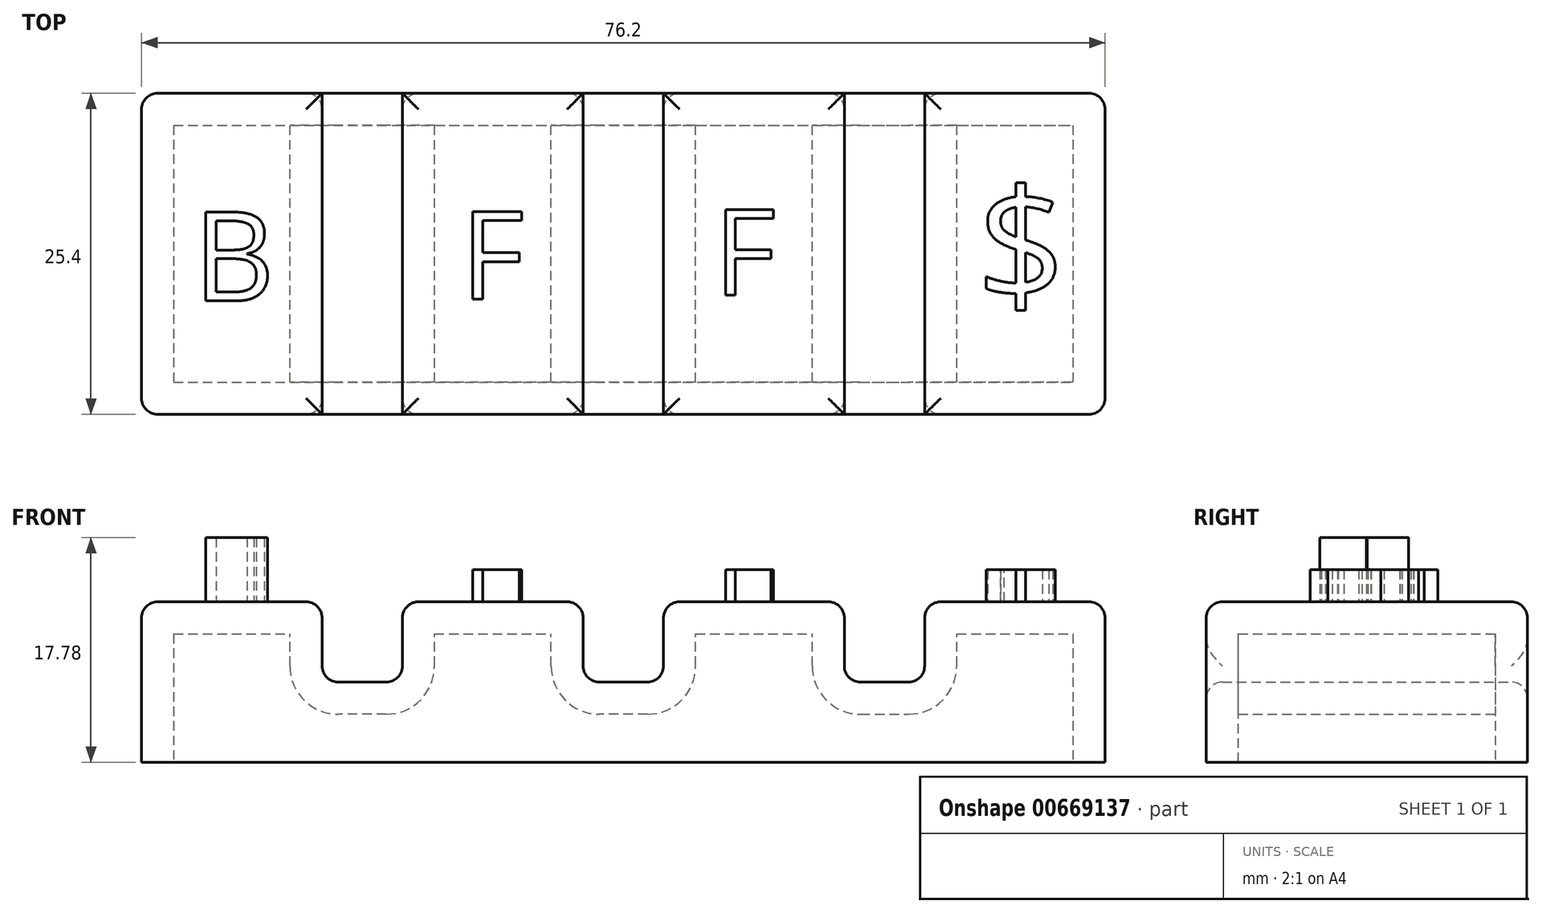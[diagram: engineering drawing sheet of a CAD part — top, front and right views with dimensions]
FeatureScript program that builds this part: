
annotation { "Feature Type Name" : "Feature", "Feature Type Description" : "" }
export const myFeature = defineFeature(function(context is Context, id is Id, definition is map)
    precondition{}
    {
        {
            var Q0;
            Q0=qCreatedBy(makeId("Top.planeOp"),FACE);
            var sketch = newSketch(context, id + "F0", { "sketchPlane" : qUnion([Q0])});
            skLineSegment(sketch, "E0.bottom", {"start": v(-38.1, 12.7) * mm, "end": v(38.1, 12.7) * mm});
            skLineSegment(sketch, "E0.top", {"start": v(-38.1, -12.7) * mm, "end": v(38.1, -12.7) * mm});
            skLineSegment(sketch, "E0.left", {"start": v(-38.1, 12.7) * mm, "end": v(-38.1, -12.7) * mm});
            skLineSegment(sketch, "E0.right", {"start": v(38.1, 12.7) * mm, "end": v(38.1, -12.7) * mm});
            skPoint(sketch, "E0.middle", {"position": v(0, 0) * mm});
            skSolve(sketch);
        }
        {
            var Q0;
            Q0 = qSketchRegion(id + "F0", true);
            extrude(context, id + "F1", {"entities" : qUnion([Q0]), "depth" : 12.7 * mm, "offsetDistance" : 25.4 * mm});
        }
        {
            var Q0;
            Q0=makeQuery(id+"F1.opExtrude","SWEPT_FACE",FACE,{"disambiguationData":[OSD([sQuery(id+"F0.wireOp",EDGE,"E0.bottom")])]});
            var sketch = newSketch(context, id + "F2", { "sketchPlane" : qUnion([Q0])});
            skLineSegment(sketch, "E1", {"start": v(-38.1, 6.35) * mm, "end": v(38.1, 6.35) * mm, "construction": true});
            skLineSegment(sketch, "E2.bottom", {"start": v(3.17, 6.35) * mm, "end": v(-3.18, 6.35) * mm});
            skLineSegment(sketch, "E2.top", {"start": v(3.17, 19.05) * mm, "end": v(-3.18, 19.05) * mm});
            skLineSegment(sketch, "E2.left", {"start": v(3.17, 6.35) * mm, "end": v(3.17, 19.05) * mm});
            skLineSegment(sketch, "E2.right", {"start": v(-3.18, 6.35) * mm, "end": v(-3.18, 19.05) * mm});
            skPoint(sketch, "E2.middle", {"position": v(0, 12.7) * mm});
            skLineSegment(sketch, "E3.bottom", {"start": v(23.83, 6.35) * mm, "end": v(17.48, 6.35) * mm});
            skLineSegment(sketch, "E3.top", {"start": v(23.83, 19.05) * mm, "end": v(17.48, 19.05) * mm});
            skLineSegment(sketch, "E3.left", {"start": v(23.83, 6.35) * mm, "end": v(23.83, 19.05) * mm});
            skLineSegment(sketch, "E3.right", {"start": v(17.48, 6.35) * mm, "end": v(17.48, 19.05) * mm});
            skPoint(sketch, "E3.middle", {"position": v(20.65, 12.7) * mm});
            skLineSegment(sketch, "E4.bottom", {"start": v(-23.83, 6.35) * mm, "end": v(-17.48, 6.35) * mm});
            skLineSegment(sketch, "E4.top", {"start": v(-23.83, 19.05) * mm, "end": v(-17.48, 19.05) * mm});
            skLineSegment(sketch, "E4.left", {"start": v(-23.83, 6.35) * mm, "end": v(-23.83, 19.05) * mm});
            skLineSegment(sketch, "E4.right", {"start": v(-17.48, 6.35) * mm, "end": v(-17.48, 19.05) * mm});
            skPoint(sketch, "E4.middle", {"position": v(-20.65, 12.7) * mm});
            skSolve(sketch);
        }
        {
            var Q0;
            Q0 = qSketchRegion(id + "F2", true);
            extrude(context, id + "F3", {"entities" : qUnion([Q0]), "operationType" : NewBodyOperationType.REMOVE, "endBound" : BoundingType.THROUGH_ALL, "oppositeDirection" : true, "depth" : 25.4 * mm, "offsetDistance" : 25.4 * mm});
        }
        {
            var Q0;
            {var subQ0=sQuery(id+"F0.wireOp",EDGE,"E0.bottom");var subQ1=sQuery(id+"F0.wireOp",EDGE,"E0.right");var subQ2=sQuery(id+"F0.wireOp",EDGE,"E0.top");Q0=makeQuery(id+"F3.boolean.opBoolean","SPLIT",FACE,{"disambiguationData":[TD([makeQuery(id+"F1.opExtrude","SWEPT_FACE",FACE,{"disambiguationData":[OSD([subQ1])]})])],"derivedFrom":makeQuery(id+"F1.opExtrude","CAP_FACE",FACE,{"disambiguationData":[OSD([subQ0,subQ2,sQuery(id+"F0.wireOp",EDGE,"E0.left"),subQ1])],"isStart":false})});}
            var Q1;
            {var subQ0=sQuery(id+"F0.wireOp",EDGE,"E0.bottom");var subQ1=sQuery(id+"F0.wireOp",EDGE,"E0.top");Q1=makeQuery(id+"F3.boolean.opBoolean","SPLIT",FACE,{"disambiguationData":[TD([makeQuery(id+"F3.opExtrude","SWEPT_FACE",FACE,{"disambiguationData":[OSD([sQuery(id+"F2.wireOp",EDGE,"E2.right")])]})])],"derivedFrom":makeQuery(id+"F1.opExtrude","CAP_FACE",FACE,{"disambiguationData":[OSD([subQ0,subQ1,sQuery(id+"F0.wireOp",EDGE,"E0.left"),sQuery(id+"F0.wireOp",EDGE,"E0.right")])],"isStart":false})});}
            var Q2;
            {var subQ0=sQuery(id+"F0.wireOp",EDGE,"E0.bottom");var subQ1=sQuery(id+"F0.wireOp",EDGE,"E0.top");Q2=makeQuery(id+"F3.boolean.opBoolean","SPLIT",FACE,{"disambiguationData":[TD([makeQuery(id+"F3.opExtrude","SWEPT_FACE",FACE,{"disambiguationData":[OSD([sQuery(id+"F2.wireOp",EDGE,"E2.left")])]})])],"derivedFrom":makeQuery(id+"F1.opExtrude","CAP_FACE",FACE,{"disambiguationData":[OSD([subQ0,subQ1,sQuery(id+"F0.wireOp",EDGE,"E0.left"),sQuery(id+"F0.wireOp",EDGE,"E0.right")])],"isStart":false})});}
            var Q3;
            Q3=makeQuery(id+"F3.boolean.opBoolean","COPY",FACE,{"derivedFrom":makeQuery(id+"F3.opExtrude","SWEPT_FACE",FACE,{"disambiguationData":[OSD([sQuery(id+"F2.wireOp",EDGE,"E4.bottom")])]})});
            var Q4;
            Q4=makeQuery(id+"F3.boolean.opBoolean","COPY",FACE,{"derivedFrom":makeQuery(id+"F3.opExtrude","SWEPT_FACE",FACE,{"disambiguationData":[OSD([sQuery(id+"F2.wireOp",EDGE,"E2.bottom")])]})});
            var Q5;
            Q5=makeQuery(id+"F3.boolean.opBoolean","COPY",FACE,{"derivedFrom":makeQuery(id+"F3.opExtrude","SWEPT_FACE",FACE,{"disambiguationData":[OSD([sQuery(id+"F2.wireOp",EDGE,"E3.bottom")])]})});
            var Q6;
            {var subQ0=sQuery(id+"F0.wireOp",EDGE,"E0.bottom");var subQ1=sQuery(id+"F0.wireOp",EDGE,"E0.top");var subQ2=sQuery(id+"F0.wireOp",EDGE,"E0.left");Q6=makeQuery(id+"F3.boolean.opBoolean","SPLIT",FACE,{"disambiguationData":[TD([makeQuery(id+"F1.opExtrude","SWEPT_FACE",FACE,{"disambiguationData":[OSD([subQ2])]})])],"derivedFrom":makeQuery(id+"F1.opExtrude","CAP_FACE",FACE,{"disambiguationData":[OSD([subQ0,subQ1,subQ2,sQuery(id+"F0.wireOp",EDGE,"E0.right")])],"isStart":false})});}
            var Q7;
            Q7=makeQuery(id+"F1.opExtrude","SWEPT_EDGE",EDGE,{"disambiguationData":[OSD([sQuery(id+"F0.wireOp",EDGE,"E0.bottom"),sQuery(id+"F0.wireOp",EDGE,"E0.left")])]});
            var Q8;
            Q8=makeQuery(id+"F1.opExtrude","SWEPT_EDGE",EDGE,{"disambiguationData":[OSD([sQuery(id+"F0.wireOp",EDGE,"E0.top"),sQuery(id+"F0.wireOp",EDGE,"E0.left")])]});
            var Q9;
            Q9=makeQuery(id+"F1.opExtrude","SWEPT_EDGE",EDGE,{"disambiguationData":[OSD([sQuery(id+"F0.wireOp",EDGE,"E0.bottom"),sQuery(id+"F0.wireOp",EDGE,"E0.right")])]});
            var Q10;
            Q10=makeQuery(id+"F1.opExtrude","SWEPT_EDGE",EDGE,{"disambiguationData":[OSD([sQuery(id+"F0.wireOp",EDGE,"E0.top"),sQuery(id+"F0.wireOp",EDGE,"E0.right")])]});
            fillet(context, id + "F4", {"entities" : qUnion([Q0, Q1, Q2, Q3, Q4, Q5, Q6, Q7, Q8, Q9, Q10]), "radius" : 1.27 * mm, "tangentPropagation" : true, "allowEdgeOverflow" : false});
        }
        {
            var Q0;
            Q0=makeQuery(id+"F1.opExtrude","CAP_FACE",FACE,{"disambiguationData":[OSD([sQuery(id+"F0.wireOp",EDGE,"E0.bottom"),sQuery(id+"F0.wireOp",EDGE,"E0.top"),sQuery(id+"F0.wireOp",EDGE,"E0.left"),sQuery(id+"F0.wireOp",EDGE,"E0.right")])],"isStart":true});
            shell(context, id + "F5", {"entities" : qUnion([Q0]), "thickness" : 2.54 * mm});
        }
        {
            var Q0;
            {var subQ0=sQuery(id+"F0.wireOp",EDGE,"E0.bottom");var subQ1=sQuery(id+"F0.wireOp",EDGE,"E0.top");var subQ2=sQuery(id+"F0.wireOp",EDGE,"E0.left");Q0=makeQuery(id+"F3.boolean.opBoolean","SPLIT",FACE,{"disambiguationData":[TD([makeQuery(id+"F1.opExtrude","SWEPT_FACE",FACE,{"disambiguationData":[OSD([subQ2])]})])],"derivedFrom":makeQuery(id+"F1.opExtrude","CAP_FACE",FACE,{"disambiguationData":[OSD([subQ0,subQ1,subQ2,sQuery(id+"F0.wireOp",EDGE,"E0.right")])],"isStart":false})});}
            var sketch = newSketch(context, id + "F6", { "sketchPlane" : qUnion([Q0])});
            skText(sketch, "E5", { "text": "B", "fontName": "OpenSans-Regular.ttf"});
            const initialGuessF6  = {"E5": [-0.03398, -0.00372, 1, 0, 0.00709]};
            skSetInitialGuess(sketch, initialGuessF6);
            skSolve(sketch);
        }
        {
            var Q0;
            Q0 = qSketchRegion(id + "F6", true);
            extrude(context, id + "F7", {"entities" : qUnion([Q0]), "operationType" : NewBodyOperationType.ADD, "depth" : 5.08 * mm, "offsetDistance" : 25.4 * mm});
        }
        {
            var Q0;
            {var subQ0=sQuery(id+"F0.wireOp",EDGE,"E0.bottom");var subQ1=sQuery(id+"F0.wireOp",EDGE,"E0.top");Q0=makeQuery(id+"F3.boolean.opBoolean","SPLIT",FACE,{"disambiguationData":[TD([makeQuery(id+"F3.opExtrude","SWEPT_FACE",FACE,{"disambiguationData":[OSD([sQuery(id+"F2.wireOp",EDGE,"E2.left")])]})])],"derivedFrom":makeQuery(id+"F1.opExtrude","CAP_FACE",FACE,{"disambiguationData":[OSD([subQ0,subQ1,sQuery(id+"F0.wireOp",EDGE,"E0.left"),sQuery(id+"F0.wireOp",EDGE,"E0.right")])],"isStart":false})});}
            var sketch = newSketch(context, id + "F8", { "sketchPlane" : qUnion([Q0])});
            skText(sketch, "E6", { "text": "F", "fontName": "OpenSans-Regular.ttf"});
            const initialGuessF8  = {"E6": [-0.01287, -0.0036, 1, 0, 0.007]};
            skSetInitialGuess(sketch, initialGuessF8);
            skSolve(sketch);
        }
        {
            var Q0;
            Q0 = qSketchRegion(id + "F8", true);
            extrude(context, id + "F9", {"entities" : qUnion([Q0]), "operationType" : NewBodyOperationType.ADD, "depth" : 2.54 * mm, "offsetDistance" : 25.4 * mm});
        }
        {
            var Q0;
            {var subQ0=sQuery(id+"F0.wireOp",EDGE,"E0.bottom");var subQ1=sQuery(id+"F0.wireOp",EDGE,"E0.top");Q0=makeQuery(id+"F3.boolean.opBoolean","SPLIT",FACE,{"disambiguationData":[TD([makeQuery(id+"F3.opExtrude","SWEPT_FACE",FACE,{"disambiguationData":[OSD([sQuery(id+"F2.wireOp",EDGE,"E2.right")])]})])],"derivedFrom":makeQuery(id+"F1.opExtrude","CAP_FACE",FACE,{"disambiguationData":[OSD([subQ0,subQ1,sQuery(id+"F0.wireOp",EDGE,"E0.left"),sQuery(id+"F0.wireOp",EDGE,"E0.right")])],"isStart":false})});}
            var sketch = newSketch(context, id + "F10", { "sketchPlane" : qUnion([Q0])});
            skText(sketch, "E7", { "text": "F", "fontName": "OpenSans-Regular.ttf"});
            const initialGuessF10  = {"E7": [0.00714, -0.00328, 1, 0, 0.00684]};
            skSetInitialGuess(sketch, initialGuessF10);
            skSolve(sketch);
        }
        {
            var Q0;
            Q0 = qSketchRegion(id + "F10", true);
            extrude(context, id + "F11", {"entities" : qUnion([Q0]), "operationType" : NewBodyOperationType.ADD, "depth" : 2.54 * mm, "offsetDistance" : 25.4 * mm});
        }
        {
            var Q0;
            {var subQ0=sQuery(id+"F0.wireOp",EDGE,"E0.bottom");var subQ1=sQuery(id+"F0.wireOp",EDGE,"E0.right");var subQ2=sQuery(id+"F0.wireOp",EDGE,"E0.top");Q0=makeQuery(id+"F3.boolean.opBoolean","SPLIT",FACE,{"disambiguationData":[TD([makeQuery(id+"F1.opExtrude","SWEPT_FACE",FACE,{"disambiguationData":[OSD([subQ1])]})])],"derivedFrom":makeQuery(id+"F1.opExtrude","CAP_FACE",FACE,{"disambiguationData":[OSD([subQ0,subQ2,sQuery(id+"F0.wireOp",EDGE,"E0.left"),subQ1])],"isStart":false})});}
            var sketch = newSketch(context, id + "F12", { "sketchPlane" : qUnion([Q0])});
            skText(sketch, "E8", { "text": "$", "fontName": "OpenSans-Regular.ttf"});
            const initialGuessF12  = {"E8": [0.0279, -0.00377, 1, 0, 0.0089]};
            skSetInitialGuess(sketch, initialGuessF12);
            skSolve(sketch);
        }
        {
            var Q0;
            Q0 = qSketchRegion(id + "F12", true);
            extrude(context, id + "F13", {"entities" : qUnion([Q0]), "operationType" : NewBodyOperationType.ADD, "depth" : 2.54 * mm, "offsetDistance" : 25.4 * mm});
        }
    });
